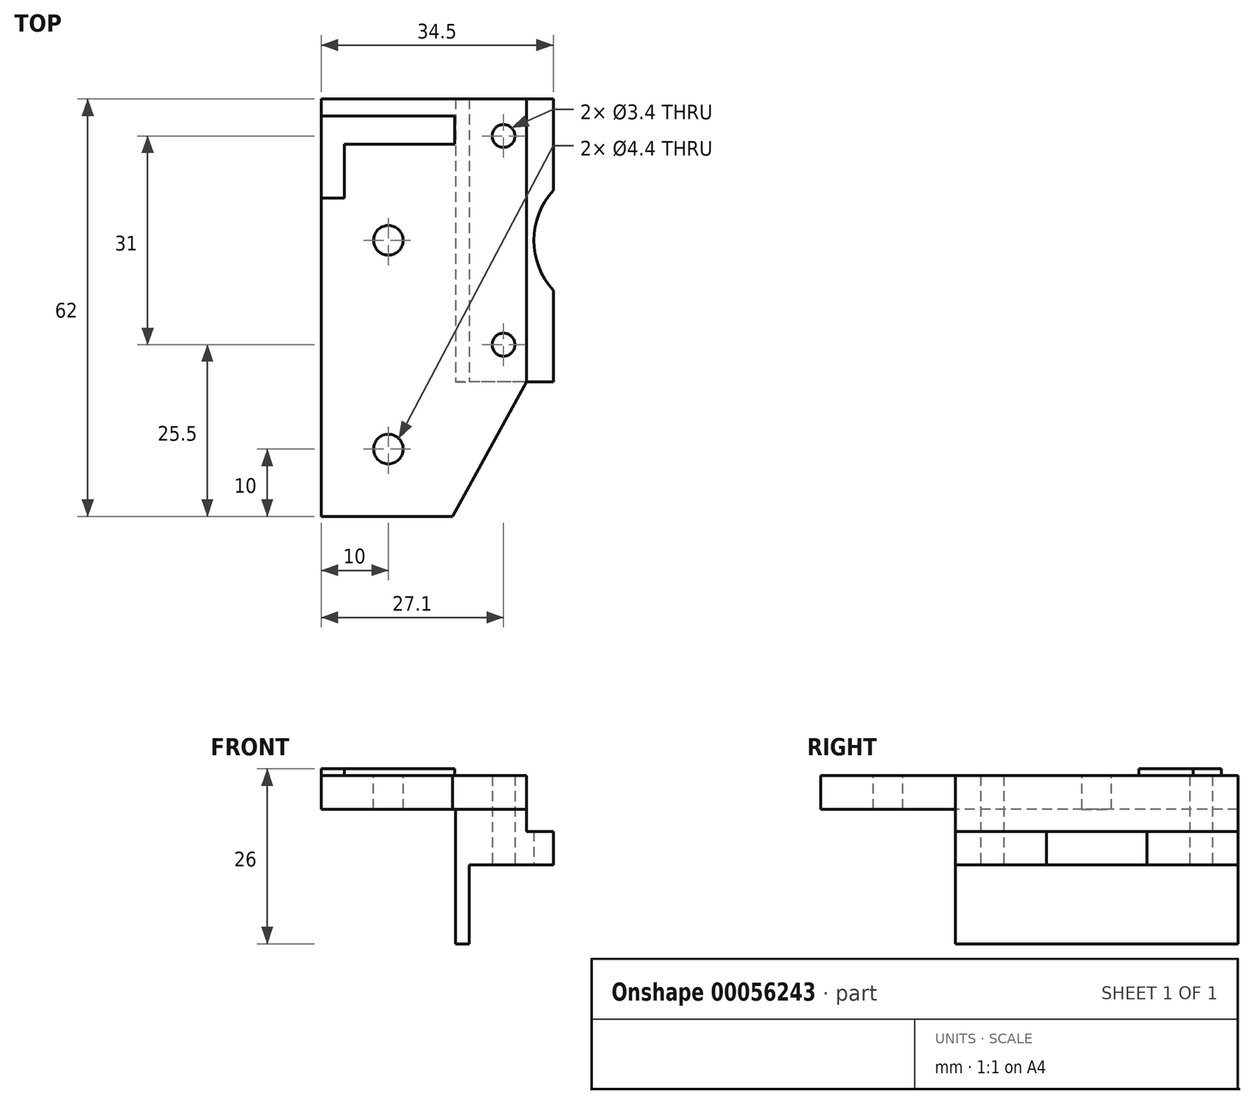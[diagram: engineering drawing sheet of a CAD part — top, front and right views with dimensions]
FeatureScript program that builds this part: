
annotation { "Feature Type Name" : "Feature", "Feature Type Description" : "" }
export const myFeature = defineFeature(function(context is Context, id is Id, definition is map)
    precondition{}
    {
        {
            var Q0;
            Q0=qCreatedBy(makeId("Front.planeOp"),FACE);
            var sketch = newSketch(context, id + "F0", { "sketchPlane" : qUnion([Q0])});
            skLineSegment(sketch, "E0", {"start": v(10.5, 13.3) * mm, "end": v(10.5, 5) * mm});
            skLineSegment(sketch, "E1", {"start": v(10.5, 5) * mm, "end": v(14.5, 5) * mm});
            skLineSegment(sketch, "E2", {"start": v(14.5, 5) * mm, "end": v(14.5, 0) * mm});
            skLineSegment(sketch, "E3", {"start": v(14.5, 0) * mm, "end": v(0, 0) * mm});
            skLineSegment(sketch, "E4", {"start": v(0, 0) * mm, "end": v(0, 13.3) * mm});
            skLineSegment(sketch, "E5", {"start": v(0, 13.3) * mm, "end": v(10.5, 13.3) * mm});
            skLineSegment(sketch, "E6", {"start": v(0, 0) * mm, "end": v(0, -11.7) * mm});
            skLineSegment(sketch, "E7", {"start": v(0, -11.7) * mm, "end": v(2, -11.7) * mm});
            skLineSegment(sketch, "E8", {"start": v(2, -11.7) * mm, "end": v(2, 0) * mm});
            skSolve(sketch);
        }
        {
            var Q0;
            Q0=qSketchRegion(id+"F0",true);
            extrude(context, id + "F1", {"entities" : qUnion([Q0]), "oppositeDirection" : true, "depth" : 42 * mm});
        }
        {
            var Q0;
            Q0=makeQuery(id+"F1.opExtrude","SWEPT_FACE",FACE,{"disambiguationData":[OSD([sQuery(id+"F0.wireOp",EDGE,"E3")])]});
            var sketch = newSketch(context, id + "F2", { "sketchPlane" : qUnion([Q0])});
            skCircle(sketch, "E9", {"center": v(7.1, -5.5) * mm, "radius": 1.7 * mm});
            skCircle(sketch, "E10", {"center": v(7.1, -36.5) * mm, "radius": 1.7 * mm});
            skCircle(sketch, "E11", {"center": v(22.6, -21) * mm, "radius": 11 * mm});
            skLineSegment(sketch, "E12", {"start": v(0, -21) * mm, "end": v(14.5, -21) * mm, "construction": true});
            skPoint(sketch, "E13", {"position": v(2, -21) * mm});
            skSolve(sketch);
        }
        {
            var Q0;
            Q0=qSketchRegion(id+"F2",true);
            extrude(context, id + "F3", {"entities" : qUnion([Q0]), "operationType" : NewBodyOperationType.REMOVE, "endBound" : BoundingType.THROUGH_ALL, "oppositeDirection" : true, "depth" : 25 * mm});
        }
        {
            var Q0;
            Q0=makeQuery(id+"F1.opExtrude","SWEPT_FACE",FACE,{"disambiguationData":[OSD([sQuery(id+"F0.wireOp",EDGE,"E4")])]});
            var sketch = newSketch(context, id + "F4", { "sketchPlane" : qUnion([Q0])});
            skLineSegment(sketch, "E14.bottom", {"start": v(-42, 13.3) * mm, "end": v(20, 13.3) * mm});
            skLineSegment(sketch, "E14.top", {"start": v(-42, 8.3) * mm, "end": v(20, 8.3) * mm});
            skLineSegment(sketch, "E14.left", {"start": v(-42, 13.3) * mm, "end": v(-42, 8.3) * mm});
            skLineSegment(sketch, "E14.right", {"start": v(20, 13.3) * mm, "end": v(20, 8.3) * mm});
            skSolve(sketch);
        }
        {
            var Q0;
            Q0=qSketchRegion(id+"F4",true);
            extrude(context, id + "F5", {"entities" : qUnion([Q0]), "operationType" : NewBodyOperationType.ADD, "depth" : 20 * mm});
        }
        {
            var Q0;
            Q0=makeQuery(id+"F5.boolean.opBoolean","MERGE",FACE,{"derivedFrom":[makeQuery(id+"F1.opExtrude","SWEPT_FACE",FACE,{"disambiguationData":[OSD([sQuery(id+"F0.wireOp",EDGE,"E5")])]}),makeQuery(id+"F5.opExtrude","SWEPT_FACE",FACE,{"disambiguationData":[OSD([sQuery(id+"F4.wireOp",EDGE,"0187bcc0-72c3-49ed-8d9d-e556f2aca4c1.bottom")])]})]});
            var sketch = newSketch(context, id + "F6", { "sketchPlane" : qUnion([Q0])});
            skCircle(sketch, "E15", {"center": v(-10, 21) * mm, "radius": 2.2 * mm});
            skCircle(sketch, "E16", {"center": v(-10, -10) * mm, "radius": 2.2 * mm});
            skPoint(sketch, "E17", {"position": v(7.1, 36.5) * mm});
            skPoint(sketch, "E18", {"position": v(7.1, 5.5) * mm});
            skLineSegment(sketch, "E19.bottom", {"start": v(-20, 42) * mm, "end": v(0, 42) * mm, "construction": true});
            skLineSegment(sketch, "E19.top", {"start": v(-20, 27) * mm, "end": v(0, 27) * mm, "construction": true});
            skLineSegment(sketch, "E19.left", {"start": v(-20, 42) * mm, "end": v(-20, 27) * mm, "construction": true});
            skLineSegment(sketch, "E19.right", {"start": v(0, 42) * mm, "end": v(0, 27) * mm, "construction": true});
            skPoint(sketch, "E20", {"position": v(10.5, 21) * mm});
            skCircle(sketch, "E21", {"center": v(-10, 21) * mm, "radius": 3.5 * mm, "construction": true});
            skSolve(sketch);
        }
        {
            var Q0;
            Q0=qSketchRegion(id+"F6",true);
            extrude(context, id + "F7", {"entities" : qUnion([Q0]), "operationType" : NewBodyOperationType.REMOVE, "endBound" : BoundingType.THROUGH_ALL, "oppositeDirection" : true, "depth" : 25 * mm, "offsetDistance" : 25 * mm});
        }
        {
            var Q0;
            Q0=makeQuery(id+"F5.boolean.opBoolean","MERGE",FACE,{"derivedFrom":[makeQuery(id+"F1.opExtrude","SWEPT_FACE",FACE,{"disambiguationData":[OSD([sQuery(id+"F0.wireOp",EDGE,"E5")])]}),makeQuery(id+"F5.opExtrude","SWEPT_FACE",FACE,{"disambiguationData":[OSD([sQuery(id+"F4.wireOp",EDGE,"0187bcc0-72c3-49ed-8d9d-e556f2aca4c1.bottom")])]})]});
            var sketch = newSketch(context, id + "F8", { "sketchPlane" : qUnion([Q0])});
            skText(sketch, "E22", { "text": "L", "fontName": "OpenSans-Bold.ttf"});
            const initialGuessF8  = {"E22": [-0.02, 0.042, 0, -1, 0.02]};
            skSetInitialGuess(sketch, initialGuessF8);
            skSolve(sketch);
        }
        {
            var Q0;
            Q0=qSketchRegion(id+"F8",true);
            extrude(context, id + "F9", {"entities" : qUnion([Q0]), "operationType" : NewBodyOperationType.ADD, "depth" : 1 * mm});
        }
        {
            var Q0;
            Q0=makeQuery(id+"F5.opExtrude","CAP_FACE",FACE,{"disambiguationData":[OSD([sQuery(id+"F4.wireOp",EDGE,"E14.bottom"),sQuery(id+"F4.wireOp",EDGE,"E14.top"),sQuery(id+"F4.wireOp",EDGE,"E14.left"),sQuery(id+"F4.wireOp",EDGE,"E14.right")])],"isStart":true});
            var Q1;
            Q1=makeQuery(id+"F1.opExtrude","SWEPT_FACE",FACE,{"disambiguationData":[OSD([sQuery(id+"F0.wireOp",EDGE,"E0")])]});
            extrude(context, id + "F10", {"entities" : qUnion([Q0]), "operationType" : NewBodyOperationType.ADD, "endBound" : BoundingType.UP_TO_SURFACE, "depth" : 25 * mm, "endBoundEntityFace" : qUnion([Q1]), "offsetDistance" : 25 * mm});
        }
        {
            var Q0;
            Q0=makeQuery(id+"F10.opExtrude","CAP_EDGE",EDGE,{"disambiguationData":[OSD([sQuery(id+"F4.wireOp",EDGE,"E14.right")])],"isStart":false});
            chamfer(context, id + "F11", {"entities" : qUnion([Q0]), "chamferType" : ChamferType.TWO_OFFSETS, "width1" : 11 * mm, "oppositeDirection" : false, "width2" : 20 * mm, "tangentPropagation" : true});
        }
    });
